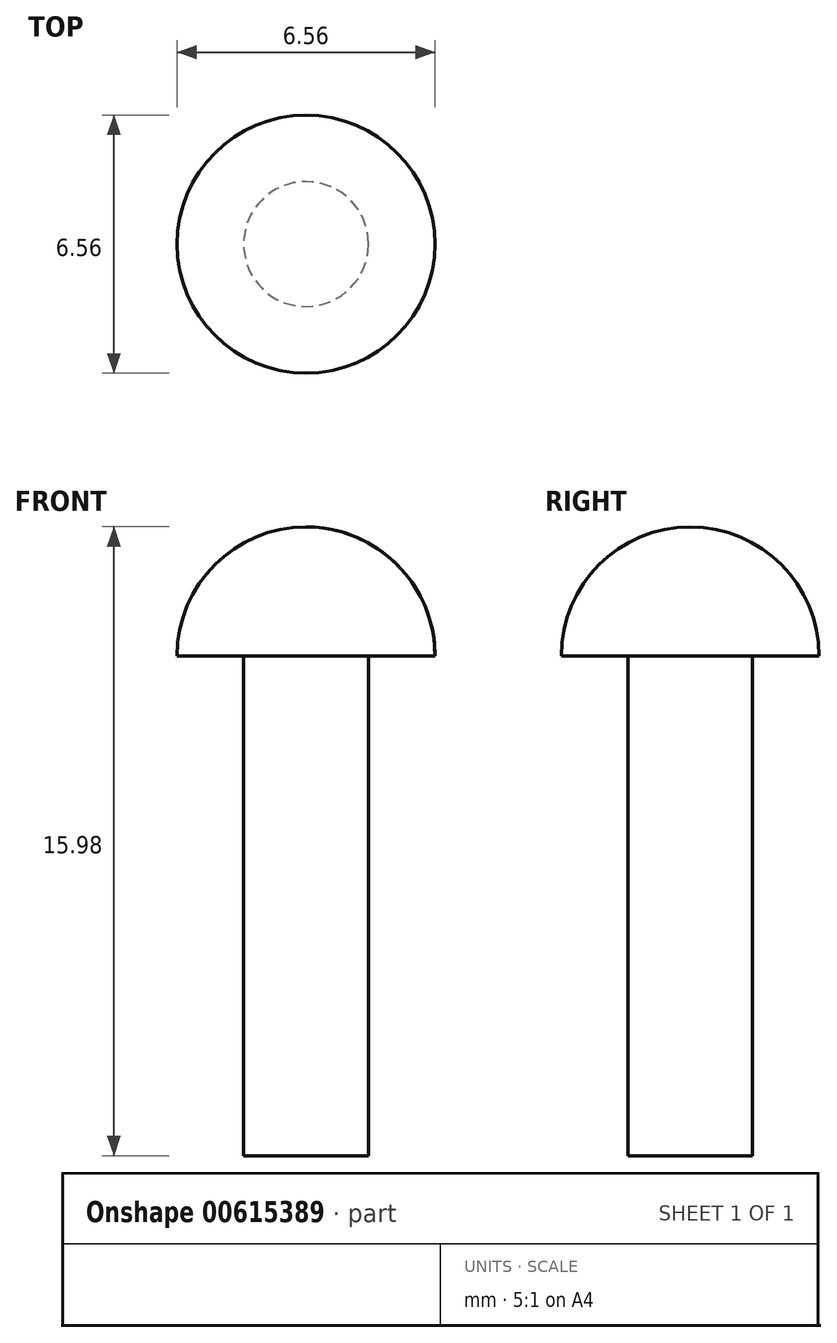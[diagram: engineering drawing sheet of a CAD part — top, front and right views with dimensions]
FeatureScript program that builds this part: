
annotation { "Feature Type Name" : "Feature", "Feature Type Description" : "" }
export const myFeature = defineFeature(function(context is Context, id is Id, definition is map)
    precondition{}
    {
        {
            var Q0;
            Q0=qCreatedBy(makeId("Front.planeOp"),FACE);
            var sketch = newSketch(context, id + "F0", { "sketchPlane" : qUnion([Q0])});
            skLineSegment(sketch, "E0", {"start": v(0, 0) * mm, "end": v(0, 12.7) * mm});
            skLineSegment(sketch, "E1", {"start": v(1.59, 12.7) * mm, "end": v(1.59, 0) * mm});
            skLineSegment(sketch, "E2", {"start": v(1.59, 0) * mm, "end": v(0, 0) * mm});
            skLineSegment(sketch, "E3", {"start": v(0, 12.7) * mm, "end": v(0, 15.98) * mm});
            skArc(sketch, "E4", {"start": v(0, 15.98) * mm, "mid": v(2.32, 15.02) * mm, "end": v(3.28, 12.7) * mm});
            skLineSegment(sketch, "E5", {"start": v(1.59, 12.7) * mm, "end": v(3.28, 12.7) * mm});
            skSolve(sketch);
        }
        {
            var Q0;
            Q0=qSketchRegion(id+"F0",true);
            var Q1;
            Q1=sQuery(id+"F0.wireOp",EDGE,"E0");
            revolve(context, id + "F1", {"entities" : qUnion([Q0]), "axis" : qUnion([Q1]), "revolveType" : RevolveType.FULL});
        }
    });
